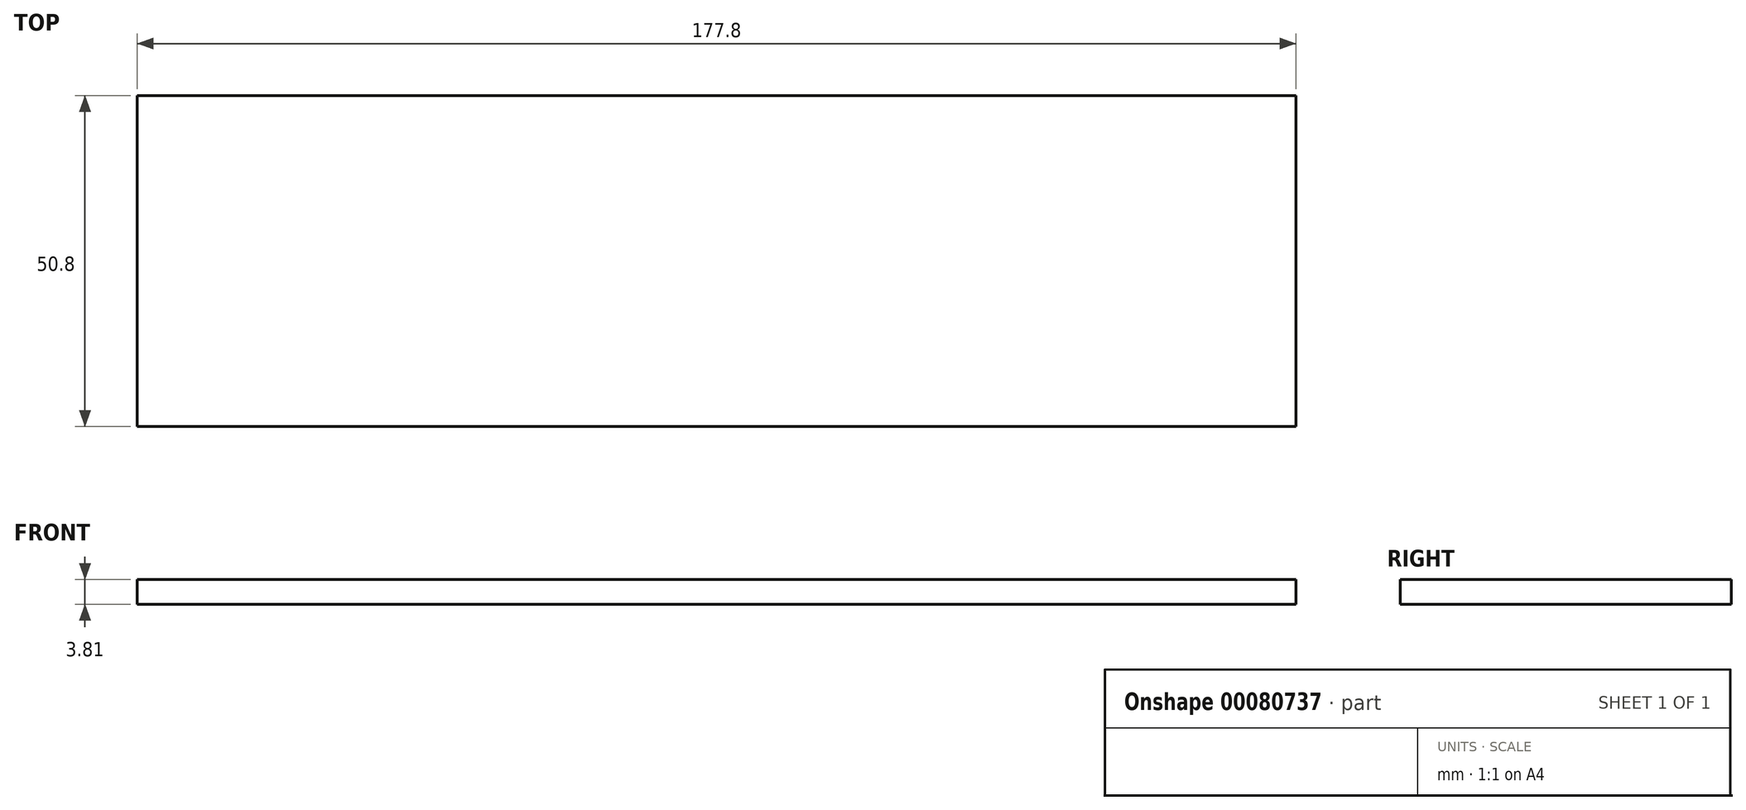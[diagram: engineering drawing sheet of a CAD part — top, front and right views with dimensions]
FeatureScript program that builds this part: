
annotation { "Feature Type Name" : "Feature", "Feature Type Description" : "" }
export const myFeature = defineFeature(function(context is Context, id is Id, definition is map)
    precondition{}
    {
        {
            var Q0;
            Q0=qCreatedBy(makeId("Top.planeOp"),FACE);
            var sketch = newSketch(context, id + "F0", { "sketchPlane" : qUnion([Q0])});
            skLineSegment(sketch, "E0.bottom", {"start": v(88.9, -25.4) * mm, "end": v(-88.9, -25.4) * mm});
            skLineSegment(sketch, "E0.top", {"start": v(88.9, 25.4) * mm, "end": v(-88.9, 25.4) * mm});
            skLineSegment(sketch, "E0.left", {"start": v(88.9, -25.4) * mm, "end": v(88.9, 25.4) * mm});
            skLineSegment(sketch, "E0.right", {"start": v(-88.9, -25.4) * mm, "end": v(-88.9, 25.4) * mm});
            skPoint(sketch, "E0.middle", {"position": v(0, 0) * mm});
            skSolve(sketch);
        }
        {
            var Q0;
            Q0=makeQuery(id+"F0.imprint","IMPRINT",FACE,{"disambiguationData":[TD([[makeQuery(id+"F0.imprint","IMPRINT",EDGE,{"derivedFrom":sQuery(id+"F0.wireOp",EDGE,"E0.bottom")}),-1.0]])]});
            extrude(context, id + "F1", {"entities" : qUnion([Q0]), "depth" : 3.8 * mm});
        }
    });
